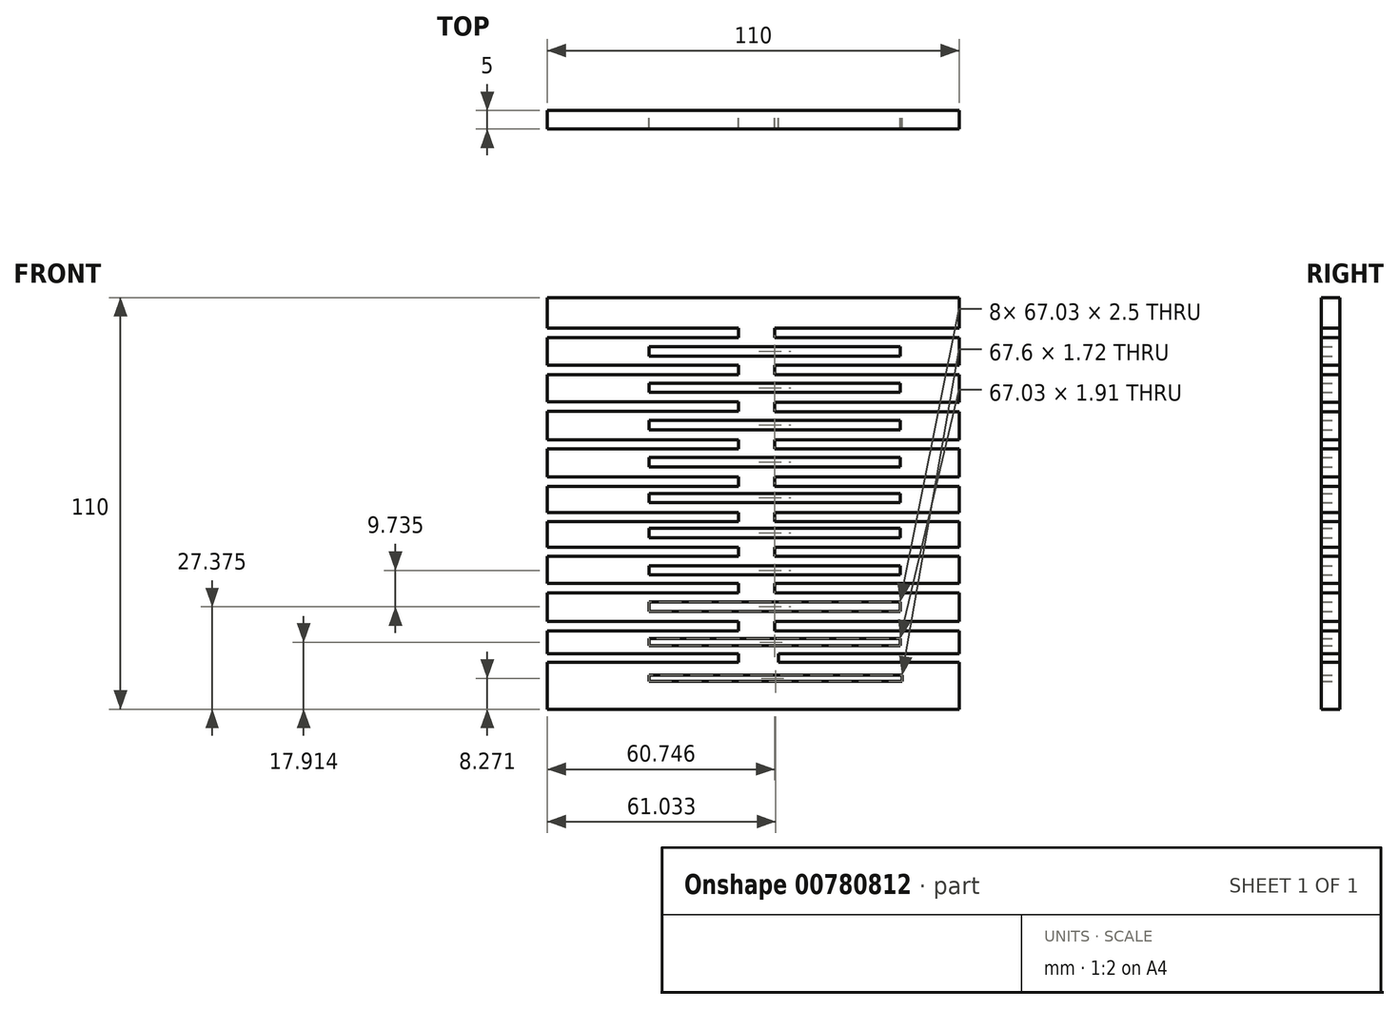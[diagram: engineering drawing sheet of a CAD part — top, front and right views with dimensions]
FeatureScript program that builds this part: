
annotation { "Feature Type Name" : "Feature", "Feature Type Description" : "" }
export const myFeature = defineFeature(function(context is Context, id is Id, definition is map)
    precondition{}
    {
        {
            var Q0;
            Q0=qCreatedBy(makeId("Front.planeOp"),FACE);
            var sketch = newSketch(context, id + "F0", { "sketchPlane" : qUnion([Q0])});
            skLineSegment(sketch, "E0.bottom", {"start": v(-55.59, 59.91) * mm, "end": v(54.41, 59.91) * mm});
            skLineSegment(sketch, "E0.top", {"start": v(-55.59, -50.09) * mm, "end": v(54.41, -50.09) * mm});
            skLineSegment(sketch, "E0.left", {"start": v(-55.59, 59.91) * mm, "end": v(-55.59, 51.75) * mm});
            skLineSegment(sketch, "E0.right", {"start": v(54.41, 59.91) * mm, "end": v(54.41, 51.75) * mm});
            skLineSegment(sketch, "E1.bottom", {"start": v(-28.36, -40.96) * mm, "end": v(39.24, -40.96) * mm});
            skLineSegment(sketch, "E1.top", {"start": v(-28.36, -42.68) * mm, "end": v(39.24, -42.68) * mm});
            skLineSegment(sketch, "E1.left", {"start": v(-28.36, -40.96) * mm, "end": v(-28.36, -42.68) * mm});
            skLineSegment(sketch, "E1.right", {"start": v(39.24, -40.96) * mm, "end": v(39.24, -42.68) * mm});
            skLineSegment(sketch, "E2.bottom", {"start": v(-55.59, -35.23) * mm, "end": v(-4.49, -35.23) * mm});
            skLineSegment(sketch, "E2.top", {"start": v(-55.59, -37.52) * mm, "end": v(-4.49, -37.52) * mm});
            skLineSegment(sketch, "E2.right", {"start": v(-4.49, -35.23) * mm, "end": v(-4.49, -37.52) * mm});
            skLineSegment(sketch, "E3.trimOffspring", {"start": v(-55.59, -37.52) * mm, "end": v(-55.59, -50.09) * mm});
            skLineSegment(sketch, "E4.bottom", {"start": v(54.41, -37.52) * mm, "end": v(6.2, -37.52) * mm});
            skLineSegment(sketch, "E4.top", {"start": v(54.41, -35.23) * mm, "end": v(6.2, -35.23) * mm});
            skLineSegment(sketch, "E4.right", {"start": v(6.2, -37.52) * mm, "end": v(6.2, -35.23) * mm});
            skLineSegment(sketch, "E5.trimOffspring", {"start": v(54.41, -37.52) * mm, "end": v(54.41, -50.09) * mm});
            skLineSegment(sketch, "E6.bottom", {"start": v(-28.36, -31.22) * mm, "end": v(38.67, -31.22) * mm});
            skLineSegment(sketch, "E6.top", {"start": v(-28.36, -33.13) * mm, "end": v(38.67, -33.13) * mm});
            skLineSegment(sketch, "E6.left", {"start": v(-28.36, -31.22) * mm, "end": v(-28.36, -33.13) * mm});
            skLineSegment(sketch, "E6.right", {"start": v(38.67, -31.22) * mm, "end": v(38.67, -33.13) * mm});
            skLineSegment(sketch, "E7.bottom", {"start": v(-4.49, -29.12) * mm, "end": v(-55.59, -29.12) * mm});
            skLineSegment(sketch, "E7.top", {"start": v(-4.49, -26.64) * mm, "end": v(-55.59, -26.64) * mm});
            skLineSegment(sketch, "E7.left", {"start": v(-4.49, -29.12) * mm, "end": v(-4.49, -26.64) * mm});
            skLineSegment(sketch, "E8.trimOffspring", {"start": v(-55.59, -29.12) * mm, "end": v(-55.59, -35.23) * mm});
            skPoint(sketch, "E9.firstSnap0", {"position": v(5.16, -31.22) * mm});
            skLineSegment(sketch, "E9.bottom", {"start": v(5.16, -29.12) * mm, "end": v(54.41, -29.12) * mm});
            skLineSegment(sketch, "E9.top", {"start": v(5.16, -26.62) * mm, "end": v(54.41, -26.62) * mm});
            skLineSegment(sketch, "E9.left", {"start": v(5.16, -29.12) * mm, "end": v(5.16, -26.62) * mm});
            skLineSegment(sketch, "E10.trimOffspring", {"start": v(54.41, -29.12) * mm, "end": v(54.41, -35.23) * mm});
            skLineSegment(sketch, "E11.bottom", {"start": v(-28.36, -23.96) * mm, "end": v(38.67, -23.96) * mm});
            skLineSegment(sketch, "E11.top", {"start": v(-28.36, -21.46) * mm, "end": v(38.67, -21.46) * mm});
            skLineSegment(sketch, "E11.left", {"start": v(-28.36, -23.96) * mm, "end": v(-28.36, -21.46) * mm});
            skLineSegment(sketch, "E11.right", {"start": v(38.67, -23.96) * mm, "end": v(38.67, -21.46) * mm});
            skLineSegment(sketch, "E12.bottom", {"start": v(-4.49, -19) * mm, "end": v(-55.59, -19) * mm});
            skLineSegment(sketch, "E12.top", {"start": v(-4.49, -16.5) * mm, "end": v(-55.59, -16.5) * mm});
            skLineSegment(sketch, "E12.left", {"start": v(-4.49, -19) * mm, "end": v(-4.49, -16.5) * mm});
            skPoint(sketch, "E13.firstSnap0", {"position": v(5.16, -21.46) * mm});
            skLineSegment(sketch, "E13.bottom", {"start": v(5.16, -19) * mm, "end": v(54.41, -19) * mm});
            skLineSegment(sketch, "E13.top", {"start": v(5.16, -16.5) * mm, "end": v(54.41, -16.5) * mm});
            skLineSegment(sketch, "E13.left", {"start": v(5.16, -19) * mm, "end": v(5.16, -16.5) * mm});
            skLineSegment(sketch, "E14.trimOffspring", {"start": v(-55.59, -19) * mm, "end": v(-55.59, -26.64) * mm});
            skLineSegment(sketch, "E15.trimOffspring", {"start": v(54.41, -19) * mm, "end": v(54.41, -26.62) * mm});
            skLineSegment(sketch, "E16.bottom", {"start": v(-28.36, -14.23) * mm, "end": v(38.67, -14.23) * mm});
            skLineSegment(sketch, "E16.top", {"start": v(-28.36, -11.73) * mm, "end": v(38.67, -11.73) * mm});
            skLineSegment(sketch, "E16.left", {"start": v(-28.36, -14.23) * mm, "end": v(-28.36, -11.73) * mm});
            skLineSegment(sketch, "E16.right", {"start": v(38.67, -14.23) * mm, "end": v(38.67, -11.73) * mm});
            skLineSegment(sketch, "E17.bottom", {"start": v(-4.49, -9.26) * mm, "end": v(-55.59, -9.26) * mm});
            skLineSegment(sketch, "E17.top", {"start": v(-4.49, -6.76) * mm, "end": v(-55.59, -6.76) * mm});
            skLineSegment(sketch, "E17.left", {"start": v(-4.49, -9.26) * mm, "end": v(-4.49, -6.76) * mm});
            skPoint(sketch, "E18.firstSnap0", {"position": v(5.16, -11.73) * mm});
            skLineSegment(sketch, "E18.bottom", {"start": v(5.16, -9.26) * mm, "end": v(54.41, -9.26) * mm});
            skLineSegment(sketch, "E18.top", {"start": v(5.16, -6.76) * mm, "end": v(54.41, -6.76) * mm});
            skLineSegment(sketch, "E18.left", {"start": v(5.16, -9.26) * mm, "end": v(5.16, -6.76) * mm});
            skLineSegment(sketch, "E19.trimOffspring", {"start": v(-55.59, -9.26) * mm, "end": v(-55.59, -16.5) * mm});
            skLineSegment(sketch, "E20.trimOffspring", {"start": v(54.41, -9.26) * mm, "end": v(54.41, -16.5) * mm});
            skLineSegment(sketch, "E21.bottom", {"start": v(-28.36, -4.29) * mm, "end": v(38.67, -4.29) * mm});
            skLineSegment(sketch, "E21.top", {"start": v(-28.36, -1.79) * mm, "end": v(38.67, -1.79) * mm});
            skLineSegment(sketch, "E21.left", {"start": v(-28.36, -4.29) * mm, "end": v(-28.36, -1.79) * mm});
            skLineSegment(sketch, "E21.right", {"start": v(38.67, -4.29) * mm, "end": v(38.67, -1.79) * mm});
            skLineSegment(sketch, "E22.bottom", {"start": v(-4.49, 0) * mm, "end": v(-55.59, 0) * mm});
            skLineSegment(sketch, "E22.top", {"start": v(-4.49, 2.5) * mm, "end": v(-55.59, 2.5) * mm});
            skLineSegment(sketch, "E22.left", {"start": v(-4.49, 0) * mm, "end": v(-4.49, 2.5) * mm});
            skLineSegment(sketch, "E23.bottom", {"start": v(5.16, 0) * mm, "end": v(54.41, 0) * mm});
            skLineSegment(sketch, "E23.top", {"start": v(5.16, 2.5) * mm, "end": v(54.41, 2.5) * mm});
            skLineSegment(sketch, "E23.left", {"start": v(5.16, 0) * mm, "end": v(5.16, 2.5) * mm});
            skLineSegment(sketch, "E24.trimOffspring", {"start": v(54.41, 0) * mm, "end": v(54.41, -6.76) * mm});
            skLineSegment(sketch, "E25.trimOffspring", {"start": v(-55.59, 0) * mm, "end": v(-55.59, -6.76) * mm});
            skLineSegment(sketch, "E26.bottom", {"start": v(-28.36, 5.08) * mm, "end": v(38.67, 5.08) * mm});
            skLineSegment(sketch, "E26.top", {"start": v(-28.36, 7.58) * mm, "end": v(38.67, 7.58) * mm});
            skLineSegment(sketch, "E26.left", {"start": v(-28.36, 5.08) * mm, "end": v(-28.36, 7.58) * mm});
            skLineSegment(sketch, "E26.right", {"start": v(38.67, 5.08) * mm, "end": v(38.67, 7.58) * mm});
            skLineSegment(sketch, "E27.bottom", {"start": v(-4.49, 9.48) * mm, "end": v(-55.59, 9.48) * mm});
            skLineSegment(sketch, "E27.top", {"start": v(-4.49, 11.98) * mm, "end": v(-55.59, 11.98) * mm});
            skLineSegment(sketch, "E27.left", {"start": v(-4.49, 9.48) * mm, "end": v(-4.49, 11.98) * mm});
            skPoint(sketch, "E28.firstSnap0", {"position": v(5.16, 7.58) * mm});
            skLineSegment(sketch, "E28.bottom", {"start": v(5.16, 9.48) * mm, "end": v(54.41, 9.48) * mm});
            skLineSegment(sketch, "E28.top", {"start": v(5.16, 11.98) * mm, "end": v(54.41, 11.98) * mm});
            skLineSegment(sketch, "E28.left", {"start": v(5.16, 9.48) * mm, "end": v(5.16, 11.98) * mm});
            skLineSegment(sketch, "E29.bottom", {"start": v(-28.36, 14.64) * mm, "end": v(38.67, 14.64) * mm});
            skLineSegment(sketch, "E29.top", {"start": v(-28.36, 17.14) * mm, "end": v(38.67, 17.14) * mm});
            skLineSegment(sketch, "E29.left", {"start": v(-28.36, 14.64) * mm, "end": v(-28.36, 17.14) * mm});
            skLineSegment(sketch, "E29.right", {"start": v(38.67, 14.64) * mm, "end": v(38.67, 17.14) * mm});
            skLineSegment(sketch, "E30.bottom", {"start": v(-4.49, 19.42) * mm, "end": v(-55.59, 19.42) * mm});
            skLineSegment(sketch, "E30.top", {"start": v(-4.49, 21.92) * mm, "end": v(-55.59, 21.92) * mm});
            skLineSegment(sketch, "E30.left", {"start": v(-4.49, 19.42) * mm, "end": v(-4.49, 21.92) * mm});
            skPoint(sketch, "E31.firstSnap0", {"position": v(5.16, 17.14) * mm});
            skLineSegment(sketch, "E31.bottom", {"start": v(5.16, 19.42) * mm, "end": v(54.41, 19.42) * mm});
            skLineSegment(sketch, "E31.top", {"start": v(5.16, 21.92) * mm, "end": v(54.41, 21.92) * mm});
            skLineSegment(sketch, "E31.left", {"start": v(5.16, 19.42) * mm, "end": v(5.16, 21.92) * mm});
            skLineSegment(sketch, "E32.bottom", {"start": v(-28.36, 24.58) * mm, "end": v(38.67, 24.58) * mm});
            skLineSegment(sketch, "E32.top", {"start": v(-28.36, 27.08) * mm, "end": v(38.67, 27.08) * mm});
            skLineSegment(sketch, "E32.left", {"start": v(-28.36, 24.58) * mm, "end": v(-28.36, 27.08) * mm});
            skLineSegment(sketch, "E32.right", {"start": v(38.67, 24.58) * mm, "end": v(38.67, 27.08) * mm});
            skLineSegment(sketch, "E33.bottom", {"start": v(-4.49, 29.55) * mm, "end": v(-55.59, 29.55) * mm});
            skLineSegment(sketch, "E33.top", {"start": v(-4.49, 32.05) * mm, "end": v(-55.59, 32.05) * mm});
            skLineSegment(sketch, "E33.left", {"start": v(-4.49, 29.55) * mm, "end": v(-4.49, 32.05) * mm});
            skLineSegment(sketch, "E34.bottom", {"start": v(5.16, 29.36) * mm, "end": v(54.41, 29.36) * mm});
            skLineSegment(sketch, "E34.top", {"start": v(5.16, 31.86) * mm, "end": v(54.41, 31.86) * mm});
            skLineSegment(sketch, "E34.left", {"start": v(5.16, 29.36) * mm, "end": v(5.16, 31.86) * mm});
            skLineSegment(sketch, "E35.bottom", {"start": v(-28.36, 34.53) * mm, "end": v(38.67, 34.53) * mm});
            skLineSegment(sketch, "E35.top", {"start": v(-28.36, 37.03) * mm, "end": v(38.67, 37.03) * mm});
            skLineSegment(sketch, "E35.left", {"start": v(-28.36, 34.53) * mm, "end": v(-28.36, 37.03) * mm});
            skLineSegment(sketch, "E35.right", {"start": v(38.67, 34.53) * mm, "end": v(38.67, 37.03) * mm});
            skLineSegment(sketch, "E36.bottom", {"start": v(-4.49, 39.3) * mm, "end": v(-55.59, 39.3) * mm});
            skLineSegment(sketch, "E36.top", {"start": v(-4.49, 41.8) * mm, "end": v(-55.59, 41.8) * mm});
            skLineSegment(sketch, "E36.left", {"start": v(-4.49, 39.3) * mm, "end": v(-4.49, 41.8) * mm});
            skPoint(sketch, "E37.firstSnap0", {"position": v(5.16, 37.03) * mm});
            skLineSegment(sketch, "E37.bottom", {"start": v(5.16, 39.3) * mm, "end": v(54.41, 39.3) * mm});
            skLineSegment(sketch, "E37.top", {"start": v(5.16, 41.8) * mm, "end": v(54.41, 41.8) * mm});
            skLineSegment(sketch, "E37.left", {"start": v(5.16, 39.3) * mm, "end": v(5.16, 41.8) * mm});
            skLineSegment(sketch, "E38.bottom", {"start": v(-28.36, 44.28) * mm, "end": v(38.67, 44.28) * mm});
            skLineSegment(sketch, "E38.top", {"start": v(-28.36, 46.78) * mm, "end": v(38.67, 46.78) * mm});
            skLineSegment(sketch, "E38.left", {"start": v(-28.36, 44.28) * mm, "end": v(-28.36, 46.78) * mm});
            skLineSegment(sketch, "E38.right", {"start": v(38.67, 44.28) * mm, "end": v(38.67, 46.78) * mm});
            skLineSegment(sketch, "E39.bottom", {"start": v(-4.49, 49.25) * mm, "end": v(-55.59, 49.25) * mm});
            skLineSegment(sketch, "E39.top", {"start": v(-4.49, 51.75) * mm, "end": v(-55.59, 51.75) * mm});
            skLineSegment(sketch, "E39.left", {"start": v(-4.49, 49.25) * mm, "end": v(-4.49, 51.75) * mm});
            skPoint(sketch, "E40.firstSnap0", {"position": v(5.16, 46.78) * mm});
            skLineSegment(sketch, "E40.bottom", {"start": v(5.16, 49.25) * mm, "end": v(54.41, 49.25) * mm});
            skLineSegment(sketch, "E40.top", {"start": v(5.16, 51.75) * mm, "end": v(54.41, 51.75) * mm});
            skLineSegment(sketch, "E40.left", {"start": v(5.16, 49.25) * mm, "end": v(5.16, 51.75) * mm});
            skLineSegment(sketch, "E41.trimOffspring", {"start": v(-55.59, 9.48) * mm, "end": v(-55.59, 2.5) * mm});
            skLineSegment(sketch, "E42.trimOffspring", {"start": v(-55.59, 19.42) * mm, "end": v(-55.59, 11.98) * mm});
            skLineSegment(sketch, "E43.trimOffspring", {"start": v(-55.59, 29.55) * mm, "end": v(-55.59, 21.92) * mm});
            skLineSegment(sketch, "E44.trimOffspring", {"start": v(-55.59, 39.3) * mm, "end": v(-55.59, 32.05) * mm});
            skLineSegment(sketch, "E45.trimOffspring", {"start": v(-55.59, 49.25) * mm, "end": v(-55.59, 41.8) * mm});
            skLineSegment(sketch, "E46.trimOffspring", {"start": v(54.41, 49.25) * mm, "end": v(54.41, 41.8) * mm});
            skLineSegment(sketch, "E47.trimOffspring", {"start": v(54.41, 39.3) * mm, "end": v(54.41, 31.86) * mm});
            skLineSegment(sketch, "E48.trimOffspring", {"start": v(54.41, 29.36) * mm, "end": v(54.41, 21.92) * mm});
            skLineSegment(sketch, "E49.trimOffspring", {"start": v(54.41, 19.42) * mm, "end": v(54.41, 11.98) * mm});
            skLineSegment(sketch, "E50.trimOffspring", {"start": v(54.41, 9.48) * mm, "end": v(54.41, 2.5) * mm});
            skSolve(sketch);
        }
        {
            var Q0;
            Q0=makeQuery(id+"F0.imprint","IMPRINT",FACE,{"disambiguationData":[TD([[makeQuery(id+"F0.imprint","IMPRINT",EDGE,{"derivedFrom":sQuery(id+"F0.wireOp",EDGE,"E0.bottom")}),-1.0]])]});
            extrude(context, id + "F1", {"entities" : qUnion([Q0]), "depth" : 5 * mm, "offsetDistance" : 25 * mm});
        }
    });
